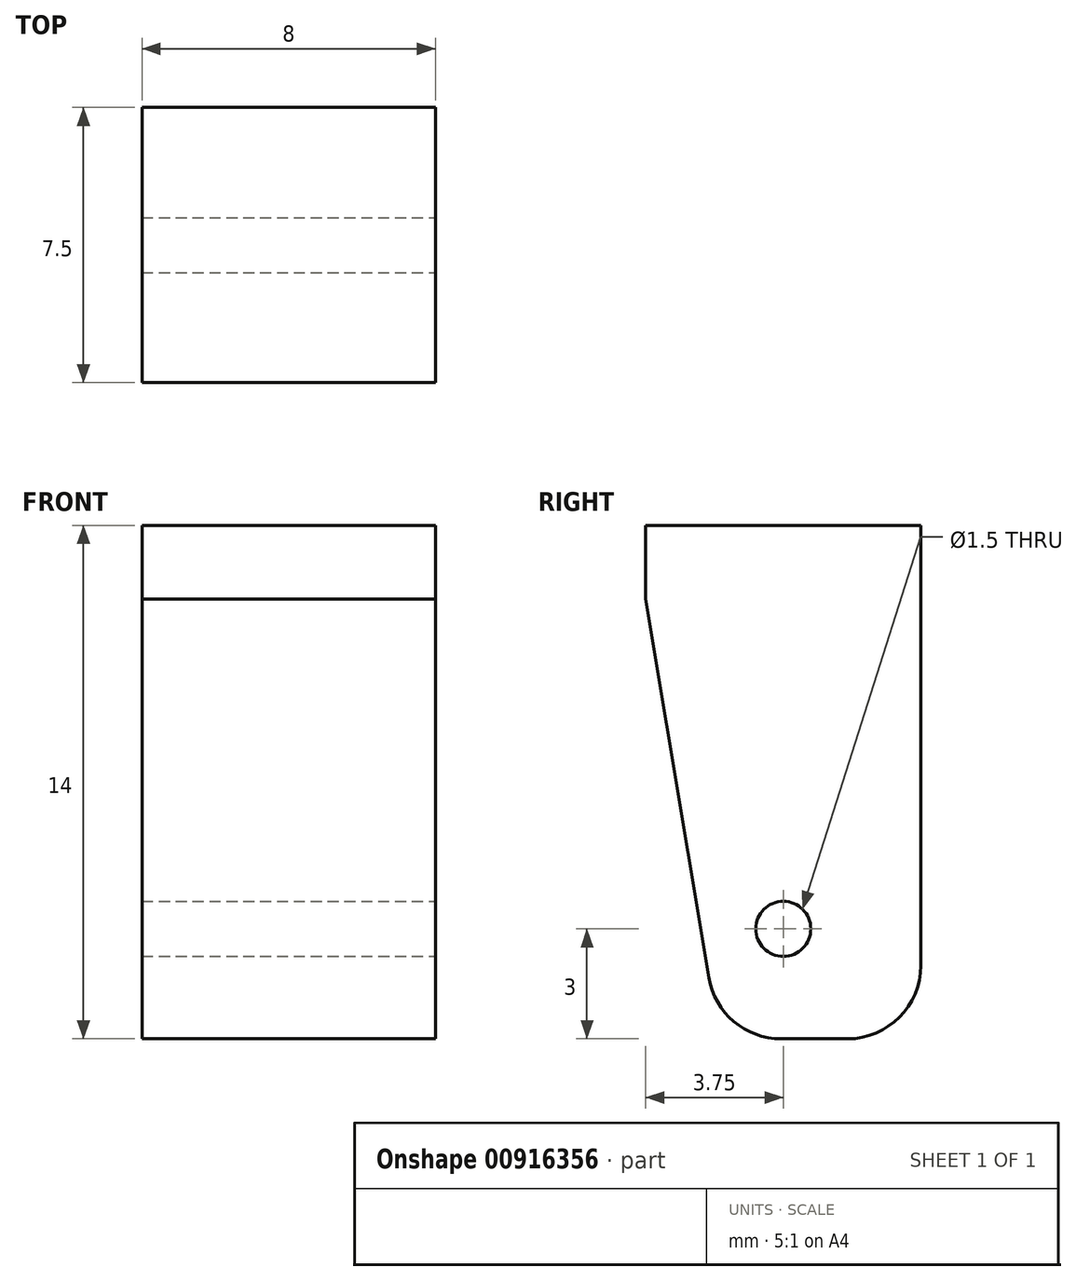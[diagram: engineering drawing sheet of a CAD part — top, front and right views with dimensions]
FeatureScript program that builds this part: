
annotation { "Feature Type Name" : "Feature", "Feature Type Description" : "" }
export const myFeature = defineFeature(function(context is Context, id is Id, definition is map)
    precondition{}
    {
        {
            var Q0;
            Q0=qCreatedBy(makeId("Top.planeOp"),FACE);
            var sketch = newSketch(context, id + "F0", { "sketchPlane" : qUnion([Q0])});
            skLineSegment(sketch, "E0.bottom", {"start": v(4, 3.75) * mm, "end": v(-4, 3.75) * mm});
            skLineSegment(sketch, "E0.top", {"start": v(4, -3.75) * mm, "end": v(-4, -3.75) * mm});
            skLineSegment(sketch, "E0.left", {"start": v(4, 3.75) * mm, "end": v(4, -3.75) * mm});
            skLineSegment(sketch, "E0.right", {"start": v(-4, 3.75) * mm, "end": v(-4, -3.75) * mm});
            skPoint(sketch, "E0.middle", {"position": v(0, 0) * mm});
            skSolve(sketch);
        }
        {
            var Q0;
            Q0=makeQuery(id+"F0.imprint","IMPRINT",FACE,{"disambiguationData":[TD([[makeQuery(id+"F0.imprint","IMPRINT",EDGE,{"derivedFrom":sQuery(id+"F0.wireOp",EDGE,"E0.bottom")}),1.0]])]});
            extrude(context, id + "F1", {"entities" : qUnion([Q0]), "depth" : 14 * mm, "offsetDistance" : 25 * mm});
        }
        {
            var Q0;
            Q0=makeQuery(id+"F1.opExtrude","SWEPT_FACE",FACE,{"disambiguationData":[OSD([sQuery(id+"F0.wireOp",EDGE,"E0.left")])]});
            var sketch = newSketch(context, id + "F2", { "sketchPlane" : qUnion([Q0])});
            skLineSegment(sketch, "E1.bottom", {"start": v(3.75, 14) * mm, "end": v(0, 14) * mm, "construction": true});
            skLineSegment(sketch, "E1.top", {"start": v(3.75, 3) * mm, "end": v(0, 3) * mm, "construction": true});
            skLineSegment(sketch, "E1.left", {"start": v(3.75, 14) * mm, "end": v(3.75, 3) * mm, "construction": true});
            skLineSegment(sketch, "E1.right", {"start": v(0, 14) * mm, "end": v(0, 3) * mm, "construction": true});
            skSolve(sketch);
        }
        {
            var Q0;
            {var subQ0=sQuery(id+"F0.wireOp",EDGE,"E0.left");Q0=makeQuery(id+"F2.imprint","IMPRINT",FACE,{"disambiguationData":[TD([[makeQuery(id+"F2.imprint","IMPRINT",EDGE,{"derivedFrom":makeQuery(id+"F1.opExtrude","CAP_EDGE",EDGE,{"disambiguationData":[OSD([subQ0])],"isStart":true})}),-1.0]])]});}
            var sketch = newSketch(context, id + "F3", { "sketchPlane" : qUnion([Q0])});
            skCircle(sketch, "E2", {"center": v(0, 3) * mm, "radius": 0.75 * mm});
            skSolve(sketch);
        }
        {
            var Q0;
            Q0 = qSketchRegion(id + "F3", true);
            extrude(context, id + "F4", {"entities" : qUnion([Q0]), "operationType" : NewBodyOperationType.REMOVE, "oppositeDirection" : true, "depth" : 8 * mm, "offsetDistance" : 25 * mm});
        }
        {
            var Q0;
            Q0=makeQuery(id+"F1.opExtrude","CAP_EDGE",EDGE,{"disambiguationData":[OSD([sQuery(id+"F0.wireOp",EDGE,"E0.top")])],"isStart":true});
            chamfer(context, id + "F5", {"entities" : qUnion([Q0]), "chamferType" : ChamferType.TWO_OFFSETS, "width1" : 2 * mm, "oppositeDirection" : false, "width2" : 12 * mm, "tangentPropagation" : true});
        }
        {
            var Q0;
            {var subQ0=sQuery(id+"F0.wireOp",EDGE,"E0.top");Q0=makeQuery(id+"F5.opChamfer","BLEND_EDGE",EDGE,{"blendedFrom":[makeQuery(id+"F1.opExtrude","CAP_EDGE",EDGE,{"disambiguationData":[OSD([subQ0])],"isStart":true}),makeQuery(id+"F1.opExtrude","CAP_FACE",FACE,{"disambiguationData":[OSD([sQuery(id+"F0.wireOp",EDGE,"E0.bottom"),subQ0,sQuery(id+"F0.wireOp",EDGE,"E0.left"),sQuery(id+"F0.wireOp",EDGE,"E0.right")])],"isStart":true})],"blendedInto":[makeQuery(id+"F1.opExtrude","CAP_FACE",FACE,{"disambiguationData":[OSD([sQuery(id+"F0.wireOp",EDGE,"E0.bottom"),subQ0,sQuery(id+"F0.wireOp",EDGE,"E0.left"),sQuery(id+"F0.wireOp",EDGE,"E0.right")])],"isStart":true})]});}
            fillet(context, id + "F6", {"entities" : qUnion([Q0]), "radius" : 2 * mm, "tangentPropagation" : true, "allowEdgeOverflow" : false});
        }
        {
            var Q0;
            Q0=makeQuery(id+"F1.opExtrude","CAP_EDGE",EDGE,{"disambiguationData":[OSD([sQuery(id+"F0.wireOp",EDGE,"E0.bottom")])],"isStart":true});
            fillet(context, id + "F7", {"entities" : qUnion([Q0]), "radius" : 2 * mm, "tangentPropagation" : true, "allowEdgeOverflow" : false});
        }
    });
